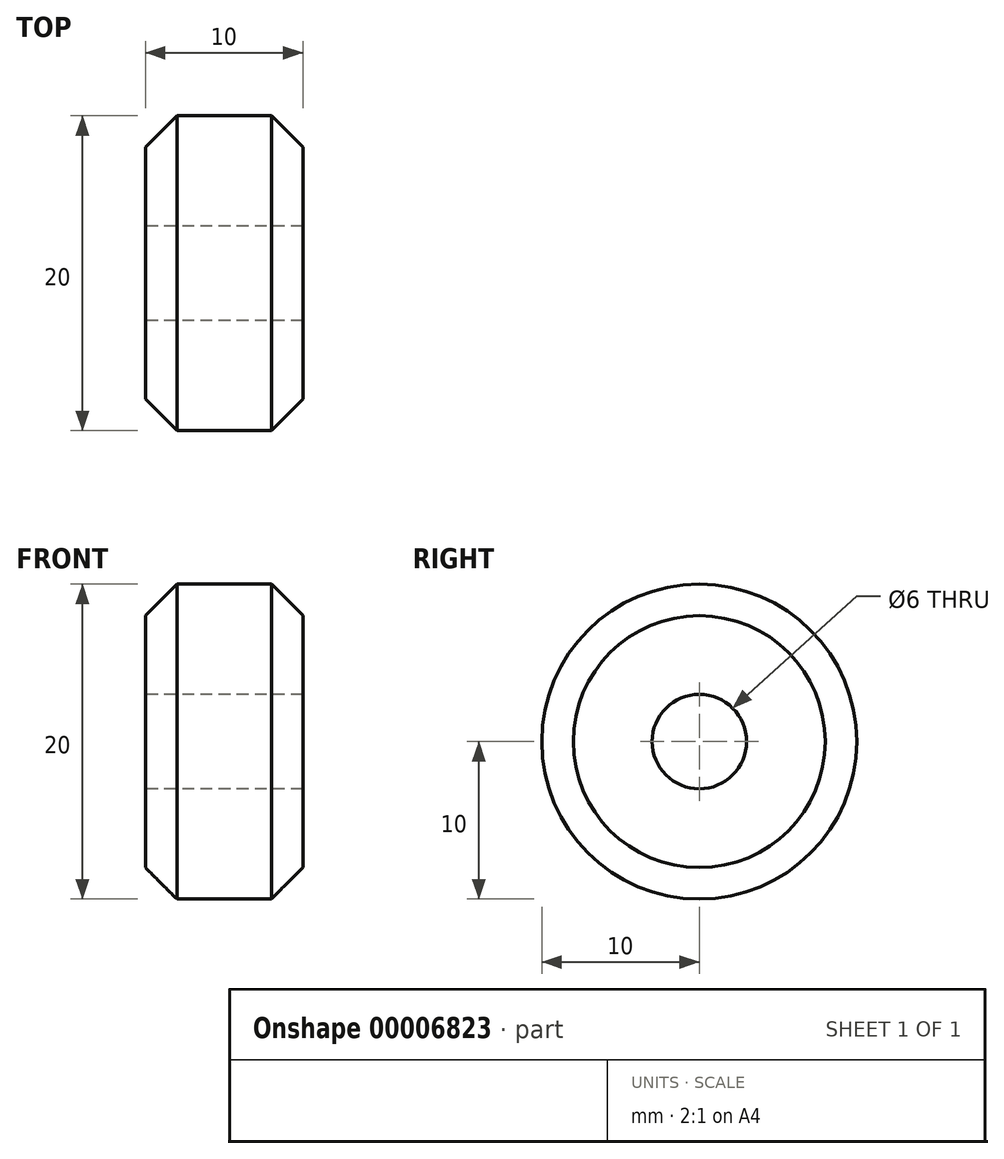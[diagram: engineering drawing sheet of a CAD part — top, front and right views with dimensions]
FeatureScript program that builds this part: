
annotation { "Feature Type Name" : "Feature", "Feature Type Description" : "" }
export const myFeature = defineFeature(function(context is Context, id is Id, definition is map)
    precondition{}
    {
        {
            var Q0;
            Q0=qCreatedBy(makeId("Right.planeOp"),FACE);
            var sketch = newSketch(context, id + "F0", { "sketchPlane" : qUnion([Q0])});
            skLineSegment(sketch, "E0", {"start": v(0, 0) * mm, "end": v(0, -3.09) * mm});
            skLineSegment(sketch, "E1", {"start": v(4.26, -9.53) * mm, "end": v(36, -23) * mm});
            skLineSegment(sketch, "E2", {"start": v(36, -23) * mm, "end": v(70, -23) * mm});
            skLineSegment(sketch, "E3", {"start": v(90, -3) * mm, "end": v(90, 47) * mm});
            skLineSegment(sketch, "E4", {"start": v(70, 67) * mm, "end": v(7, 67) * mm});
            skLineSegment(sketch, "E5", {"start": v(7, 67) * mm, "end": v(7, 45) * mm});
            skLineSegment(sketch, "E6", {"start": v(7, 45) * mm, "end": v(61, 45) * mm});
            skLineSegment(sketch, "E7", {"start": v(68, 38) * mm, "end": v(68, 4) * mm});
            skLineSegment(sketch, "E8", {"start": v(61, -3) * mm, "end": v(36, -3) * mm});
            skLineSegment(sketch, "E9", {"start": v(36, -3) * mm, "end": v(36, 0) * mm});
            skLineSegment(sketch, "E10", {"start": v(36, 0) * mm, "end": v(0, 0) * mm});
            skLineSegment(sketch, "E11", {"start": v(36, -23) * mm, "end": v(21.85, -23) * mm, "construction": true});
            skPoint(sketch, "E12.visualSharp", {"position": v(90, -23) * mm});
            skArc(sketch, "E12.filletArc", {"start": v(70, -23) * mm, "mid": v(84.14, -17.14) * mm, "end": v(90, -3) * mm});
            skPoint(sketch, "E13.visualSharp", {"position": v(90, 67) * mm});
            skArc(sketch, "E13.filletArc", {"start": v(90, 47) * mm, "mid": v(84.14, 61.14) * mm, "end": v(70, 67) * mm});
            skPoint(sketch, "E14.visualSharp", {"position": v(68, 45) * mm});
            skArc(sketch, "E14.filletArc", {"start": v(68, 38) * mm, "mid": v(65.95, 42.95) * mm, "end": v(61, 45) * mm});
            skPoint(sketch, "E15.visualSharp", {"position": v(68, -3) * mm});
            skArc(sketch, "E15.filletArc", {"start": v(61, -3) * mm, "mid": v(65.95, -0.95) * mm, "end": v(68, 4) * mm});
            skPoint(sketch, "E16.visualSharp", {"position": v(0, -7.72) * mm});
            skArc(sketch, "E16.filletArc", {"start": v(0, -3.09) * mm, "mid": v(1.16, -6.95) * mm, "end": v(4.26, -9.53) * mm});
            skSolve(sketch);
        }
        {
            var Q0;
            Q0=qSketchRegion(id+"F0",true);
            extrude(context, id + "F1", {"entities" : qUnion([Q0]), "endBound" : BoundingType.SYMMETRIC, "depth" : 20 * mm});
        }
        {
            var Q0;
            Q0=makeQuery(id+"F1.opExtrude","SWEPT_FACE",FACE,{"disambiguationData":[OSD([sQuery(id+"F0.wireOp",EDGE,"E6")])]});
            var sketch = newSketch(context, id + "F2", { "sketchPlane" : qUnion([Q0])});
            skCircle(sketch, "E17", {"center": v(0, -18) * mm, "radius": 11 * mm});
            skCircle(sketch, "E18", {"center": v(0, -18) * mm, "radius": 7 * mm});
            skSolve(sketch);
        }
        {
            var Q0;
            Q0=qSketchRegion(id+"F2",true);
            extrude(context, id + "F3", {"entities" : qUnion([Q0]), "operationType" : NewBodyOperationType.ADD, "oppositeDirection" : true, "depth" : 25 * mm});
        }
        {
            var Q0;
            Q0=makeQuery(id+"F3.boolean.opBoolean","SPLIT",FACE,{"disambiguationData":[TD([makeQuery(id+"F3.opExtrude","SWEPT_FACE",FACE,{"disambiguationData":[OSD([sQuery(id+"F2.wireOp",EDGE,"E18")])]})])],"derivedFrom":makeQuery(id+"F1.opExtrude","SWEPT_FACE",FACE,{"disambiguationData":[OSD([sQuery(id+"F0.wireOp",EDGE,"E4")])]})});
            var sketch = newSketch(context, id + "F4", { "sketchPlane" : qUnion([Q0])});
            skCircle(sketch, "E19.0", {"center": v(0, 18) * mm, "radius": 7 * mm});
            skSolve(sketch);
        }
        {
            var Q0;
            Q0=qSketchRegion(id+"F4",true);
            extrude(context, id + "F5", {"entities" : qUnion([Q0]), "operationType" : NewBodyOperationType.REMOVE, "oppositeDirection" : true, "depth" : 25 * mm});
        }
        {
            var Q0;
            {var subQ0=sQuery(id+"F0.wireOp",EDGE,"E4");var subQ1=makeQuery(id+"F1.opExtrude","SWEPT_FACE",FACE,{"disambiguationData":[OSD([subQ0])]});var subQ2=sQuery(id+"F0.wireOp",EDGE,"E5");Q0=makeQuery(id+"F3.boolean.opBoolean","SPLIT",FACE,{"disambiguationData":[TD([makeQuery(id+"F1.opExtrude","CAP_FACE",FACE,{"disambiguationData":[OSD([sQuery(id+"F0.wireOp",EDGE,"E0"),sQuery(id+"F0.wireOp",EDGE,"E1"),sQuery(id+"F0.wireOp",EDGE,"E2"),sQuery(id+"F0.wireOp",EDGE,"E3"),subQ0,subQ2,sQuery(id+"F0.wireOp",EDGE,"E6"),sQuery(id+"F0.wireOp",EDGE,"E7"),sQuery(id+"F0.wireOp",EDGE,"E8"),sQuery(id+"F0.wireOp",EDGE,"E9"),sQuery(id+"F0.wireOp",EDGE,"E10"),sQuery(id+"F0.wireOp",EDGE,"E12.filletArc"),sQuery(id+"F0.wireOp",EDGE,"E13.filletArc"),sQuery(id+"F0.wireOp",EDGE,"E14.filletArc"),sQuery(id+"F0.wireOp",EDGE,"E15.filletArc"),sQuery(id+"F0.wireOp",EDGE,"E16.filletArc")])],"isStart":false}),subQ1,makeQuery(id+"F1.opExtrude","SWEPT_FACE",FACE,{"disambiguationData":[OSD([subQ2])]}),makeQuery(id+"F3.opExtrude","SWEPT_FACE",FACE,{"disambiguationData":[OSD([sQuery(id+"F2.wireOp",EDGE,"E17")])]})])],"derivedFrom":subQ1});}
            var sketch = newSketch(context, id + "F6", { "sketchPlane" : qUnion([Q0])});
            skLineSegment(sketch, "E20.1.0", {"start": v(-10, 7) * mm, "end": v(0, 7) * mm});
            skArc(sketch, "E20.1.1", {"start": v(0, 7) * mm, "mid": v(-5.94, 8.74) * mm, "end": v(-10, 13.42) * mm});
            skLineSegment(sketch, "E20.1.2", {"start": v(-10, 13.42) * mm, "end": v(-10, 7) * mm});
            skSolve(sketch);
        }
        {
            var Q0;
            Q0=qSketchRegion(id+"F6",true);
            extrude(context, id + "F7", {"entities" : qUnion([Q0]), "operationType" : NewBodyOperationType.REMOVE, "oppositeDirection" : true, "depth" : 25 * mm});
        }
        {
            var Q0;
            {var subQ0=sQuery(id+"F0.wireOp",EDGE,"E4");var subQ1=makeQuery(id+"F1.opExtrude","SWEPT_FACE",FACE,{"disambiguationData":[OSD([subQ0])]});var subQ2=sQuery(id+"F0.wireOp",EDGE,"E5");Q0=makeQuery(id+"F3.boolean.opBoolean","SPLIT",FACE,{"disambiguationData":[TD([makeQuery(id+"F1.opExtrude","CAP_FACE",FACE,{"disambiguationData":[OSD([sQuery(id+"F0.wireOp",EDGE,"E0"),sQuery(id+"F0.wireOp",EDGE,"E1"),sQuery(id+"F0.wireOp",EDGE,"E2"),sQuery(id+"F0.wireOp",EDGE,"E3"),subQ0,subQ2,sQuery(id+"F0.wireOp",EDGE,"E6"),sQuery(id+"F0.wireOp",EDGE,"E7"),sQuery(id+"F0.wireOp",EDGE,"E8"),sQuery(id+"F0.wireOp",EDGE,"E9"),sQuery(id+"F0.wireOp",EDGE,"E10"),sQuery(id+"F0.wireOp",EDGE,"E12.filletArc"),sQuery(id+"F0.wireOp",EDGE,"E13.filletArc"),sQuery(id+"F0.wireOp",EDGE,"E14.filletArc"),sQuery(id+"F0.wireOp",EDGE,"E15.filletArc"),sQuery(id+"F0.wireOp",EDGE,"E16.filletArc")])],"isStart":false}),subQ1,makeQuery(id+"F1.opExtrude","SWEPT_FACE",FACE,{"disambiguationData":[OSD([subQ2])]}),makeQuery(id+"F3.opExtrude","SWEPT_FACE",FACE,{"disambiguationData":[OSD([sQuery(id+"F2.wireOp",EDGE,"E17")])]})])],"derivedFrom":subQ1});}
            var sketch = newSketch(context, id + "F8", { "sketchPlane" : qUnion([Q0])});
            skArc(sketch, "E21.0", {"start": v(10, 13.42) * mm, "mid": v(5.94, 8.74) * mm, "end": v(0, 7) * mm});
            skLineSegment(sketch, "E22", {"start": v(10, 13.42) * mm, "end": v(10, 7) * mm});
            skLineSegment(sketch, "E23", {"start": v(10, 7) * mm, "end": v(0, 7) * mm});
            skSolve(sketch);
        }
        {
            var Q0;
            Q0=qSketchRegion(id+"F8",true);
            extrude(context, id + "F9", {"entities" : qUnion([Q0]), "operationType" : NewBodyOperationType.REMOVE, "oppositeDirection" : true, "depth" : 25 * mm});
        }
        {
            var Q0;
            Q0=makeQuery(id+"F1.opExtrude","SWEPT_EDGE",EDGE,{"disambiguationData":[OSD([sQuery(id+"F0.wireOp",EDGE,"E8"),sQuery(id+"F0.wireOp",EDGE,"E9")])]});
            fillet(context, id + "F10", {"entities" : qUnion([Q0]), "radius" : 3 * mm, "tangentPropagation" : true, "allowEdgeOverflow" : false});
        }
        {
            var Q0;
            Q0=qCreatedBy(makeId("Right.planeOp"),FACE);
            var sketch = newSketch(context, id + "F11", { "sketchPlane" : qUnion([Q0])});
            skLineSegment(sketch, "E24", {"start": v(11, 100) * mm, "end": v(7, 100) * mm});
            skLineSegment(sketch, "E25", {"start": v(7, 100) * mm, "end": v(7, 118) * mm});
            skLineSegment(sketch, "E26", {"start": v(7, 118) * mm, "end": v(18, 118) * mm});
            skLineSegment(sketch, "E27", {"start": v(18, 118) * mm, "end": v(18, 35) * mm});
            skLineSegment(sketch, "E28", {"start": v(11, 100) * mm, "end": v(11, 35) * mm});
            skLineSegment(sketch, "E29", {"start": v(11, 35) * mm, "end": v(18, 35) * mm});
            skSolve(sketch);
        }
        {
            var Q0;
            Q0=qSketchRegion(id+"F11",true);
            var Q1;
            Q1=sQuery(id+"F11.wireOp",EDGE,"E27");
            revolve(context, id + "F12", {"entities" : qUnion([Q0]), "axis" : qUnion([Q1]), "revolveType" : RevolveType.FULL});
        }
        {
            var Q0;
            Q0=makeQuery(id+"F12.opRevolve","SWEPT_EDGE",EDGE,{"disambiguationData":[OSD([sQuery(id+"F11.wireOp",EDGE,"E25"),sQuery(id+"F11.wireOp",EDGE,"E26")])]});
            chamfer(context, id + "F13", {"entities" : qUnion([Q0]), "width" : 2 * mm, "tangentPropagation" : true});
        }
        {
            var Q0;
            Q0=makeQuery(id+"F12.opRevolve","SWEPT_FACE",FACE,{"disambiguationData":[OSD([sQuery(id+"F11.wireOp",EDGE,"E29")])]});
            var sketch = newSketch(context, id + "F14", { "sketchPlane" : qUnion([Q0])});
            skCircle(sketch, "E30", {"center": v(0, -18) * mm, "radius": 5 * mm});
            skSolve(sketch);
        }
        {
            var Q0;
            Q0=qSketchRegion(id+"F14",true);
            extrude(context, id + "F15", {"entities" : qUnion([Q0]), "operationType" : NewBodyOperationType.ADD, "depth" : 2 * mm});
        }
        {
            var Q0;
            Q0=makeQuery(id+"F15.opExtrude","CAP_FACE",FACE,{"disambiguationData":[OSD([sQuery(id+"F14.wireOp",EDGE,"E30")])],"isStart":false});
            var sketch = newSketch(context, id + "F16", { "sketchPlane" : qUnion([Q0])});
            skCircle(sketch, "E31", {"center": v(0, -18) * mm, "radius": 3 * mm});
            skSolve(sketch);
        }
        {
            var Q0;
            Q0=qSketchRegion(id+"F16",true);
            extrude(context, id + "F17", {"entities" : qUnion([Q0]), "operationType" : NewBodyOperationType.ADD, "depth" : 8 * mm});
        }
        {
            var Q0;
            Q0=qCreatedBy(makeId("Right.planeOp"),FACE);
            var sketch = newSketch(context, id + "F18", { "sketchPlane" : qUnion([Q0])});
            skCircle(sketch, "E32", {"center": v(18, 109) * mm, "radius": 5 * mm});
            skSolve(sketch);
        }
        {
            var Q0;
            Q0=qSketchRegion(id+"F18",true);
            extrude(context, id + "F19", {"entities" : qUnion([Q0]), "operationType" : NewBodyOperationType.REMOVE, "oppositeDirection" : true, "depth" : 25 * mm});
        }
        {
            var Q0;
            Q0=makeQuery(id+"F19.boolean.opBoolean","COPY",FACE,{"derivedFrom":makeQuery(id+"F19.opExtrude","CAP_FACE",FACE,{"disambiguationData":[OSD([sQuery(id+"F18.wireOp",EDGE,"E32")])],"isStart":true})});
            var sketch = newSketch(context, id + "F20", { "sketchPlane" : qUnion([Q0])});
            skCircle(sketch, "E33.0", {"center": v(-18, 109) * mm, "radius": 5 * mm});
            skSolve(sketch);
        }
        {
            var Q0;
            Q0=qSketchRegion(id+"F20",true);
            extrude(context, id + "F21", {"entities" : qUnion([Q0]), "operationType" : NewBodyOperationType.REMOVE, "oppositeDirection" : true, "depth" : 25 * mm});
        }
        {
            var Q0;
            Q0=qCreatedBy(makeId("Right.planeOp"),FACE);
            var sketch = newSketch(context, id + "F22", { "sketchPlane" : qUnion([Q0])});
            skCircle(sketch, "E34.0", {"center": v(18, 109) * mm, "radius": 5 * mm});
            skSolve(sketch);
        }
        {
            var Q0;
            Q0=qSketchRegion(id+"F22",true);
            extrude(context, id + "F23", {"entities" : qUnion([Q0]), "endBound" : BoundingType.SYMMETRIC, "depth" : 89 * mm});
        }
        {
            var Q0;
            Q0=makeQuery(id+"F23.opExtrude","CAP_FACE",FACE,{"disambiguationData":[OSD([sQuery(id+"F22.wireOp",EDGE,"E34.0")])],"isStart":false});
            var sketch = newSketch(context, id + "F24", { "sketchPlane" : qUnion([Q0])});
            skCircle(sketch, "E35", {"center": v(18, 109) * mm, "radius": 3 * mm});
            skSolve(sketch);
        }
        {
            var Q0;
            Q0=qSketchRegion(id+"F24",true);
            extrude(context, id + "F25", {"entities" : qUnion([Q0]), "operationType" : NewBodyOperationType.ADD, "depth" : 12 * mm});
        }
        {
            var Q0;
            Q0=makeQuery(id+"F23.opExtrude","CAP_FACE",FACE,{"disambiguationData":[OSD([sQuery(id+"F22.wireOp",EDGE,"E34.0")])],"isStart":true});
            var sketch = newSketch(context, id + "F26", { "sketchPlane" : qUnion([Q0])});
            skCircle(sketch, "E36", {"center": v(-18, 109) * mm, "radius": 3 * mm});
            skSolve(sketch);
        }
        {
            var Q0;
            Q0=qSketchRegion(id+"F26",true);
            extrude(context, id + "F27", {"entities" : qUnion([Q0]), "operationType" : NewBodyOperationType.ADD, "depth" : 12 * mm});
        }
        {
            var Q0;
            Q0=makeQuery(id+"F25.opExtrude","CAP_FACE",FACE,{"disambiguationData":[OSD([sQuery(id+"F24.wireOp",EDGE,"E35")])],"isStart":false});
            var sketch = newSketch(context, id + "F28", { "sketchPlane" : qUnion([Q0])});
            skCircle(sketch, "E37.0", {"center": v(18, 109) * mm, "radius": 3 * mm});
            skCircle(sketch, "E38", {"center": v(18, 109) * mm, "radius": 10 * mm});
            skSolve(sketch);
        }
        {
            var Q0;
            Q0=qSketchRegion(id+"F28",true);
            extrude(context, id + "F29", {"entities" : qUnion([Q0]), "oppositeDirection" : true, "depth" : 10 * mm});
        }
        {
            var Q0;
            Q0=makeQuery(id+"F29.opExtrude","CAP_EDGE",EDGE,{"disambiguationData":[OSD([sQuery(id+"F28.wireOp",EDGE,"E38")])],"isStart":true});
            var Q1;
            Q1=makeQuery(id+"F29.opExtrude","CAP_EDGE",EDGE,{"disambiguationData":[OSD([sQuery(id+"F28.wireOp",EDGE,"E38")])],"isStart":false});
            chamfer(context, id + "F30", {"entities" : qUnion([Q0, Q1]), "width" : 2 * mm, "tangentPropagation" : true});
        }
        {
            var Q0;
            Q0=makeQuery(id+"F29.opExtrude","SWEPT_BODY",BODY,{"disambiguationData":[OSD([sQuery(id+"F28.wireOp",EDGE,"E37.0"),sQuery(id+"F28.wireOp",EDGE,"E38")])]});
            var Q1;
            Q1=qCreatedBy(makeId("Right.planeOp"),FACE);
            mirror(context, id + "F31", {"entities" : qUnion([Q0]), "mirrorPlane" : qUnion([Q1])});
        }
        {
            var Q0;
            Q0=qCreatedBy(makeId("Right.planeOp"),FACE);
            var sketch = newSketch(context, id + "F32", { "sketchPlane" : qUnion([Q0])});
            skLineSegment(sketch, "E39", {"start": v(21, 30) * mm, "end": v(21, 32) * mm});
            skLineSegment(sketch, "E40", {"start": v(34.36, 22) * mm, "end": v(36.5, 22) * mm});
            skArc(sketch, "E41", {"start": v(36.5, 22) * mm, "mid": v(30.47, 29.67) * mm, "end": v(21, 32) * mm});
            skArc(sketch, "E42.0", {"start": v(34.36, 22) * mm, "mid": v(29, 28.23) * mm, "end": v(21, 30) * mm});
            skLineSegment(sketch, "E43", {"start": v(18, 24.98) * mm, "end": v(18, 32) * mm});
            skSolve(sketch);
        }
        {
            var Q0;
            Q0=qSketchRegion(id+"F32",true);
            var Q1;
            Q1=sQuery(id+"F32.wireOp",EDGE,"E43");
            revolve(context, id + "F33", {"entities" : qUnion([Q0]), "axis" : qUnion([Q1]), "revolveType" : RevolveType.FULL});
        }
        {
            var Q0;
            Q0=makeQuery(id+"F1.opExtrude","SWEPT_BODY",BODY,{"disambiguationData":[OSD([sQuery(id+"F0.wireOp",EDGE,"E0"),sQuery(id+"F0.wireOp",EDGE,"E1"),sQuery(id+"F0.wireOp",EDGE,"E2"),sQuery(id+"F0.wireOp",EDGE,"E3"),sQuery(id+"F0.wireOp",EDGE,"E4"),sQuery(id+"F0.wireOp",EDGE,"E5"),sQuery(id+"F0.wireOp",EDGE,"E6"),sQuery(id+"F0.wireOp",EDGE,"E7"),sQuery(id+"F0.wireOp",EDGE,"E8"),sQuery(id+"F0.wireOp",EDGE,"E9"),sQuery(id+"F0.wireOp",EDGE,"E10"),sQuery(id+"F0.wireOp",EDGE,"E12.filletArc"),sQuery(id+"F0.wireOp",EDGE,"E13.filletArc"),sQuery(id+"F0.wireOp",EDGE,"E14.filletArc"),sQuery(id+"F0.wireOp",EDGE,"E15.filletArc"),sQuery(id+"F0.wireOp",EDGE,"E16.filletArc")])]});
            deleteBodies(context, id + "F34", {"entities" : qUnion([Q0])});
        }
        {
            var Q0;
            Q0=makeQuery(id+"F12.opRevolve","SWEPT_BODY",BODY,{"disambiguationData":[OSD([sQuery(id+"F11.wireOp",EDGE,"E24"),sQuery(id+"F11.wireOp",EDGE,"E25"),sQuery(id+"F11.wireOp",EDGE,"E26"),sQuery(id+"F11.wireOp",EDGE,"E27"),sQuery(id+"F11.wireOp",EDGE,"E28"),sQuery(id+"F11.wireOp",EDGE,"E29")])]});
            deleteBodies(context, id + "F35", {"entities" : qUnion([Q0])});
        }
        {
            var Q0;
            Q0=makeQuery(id+"F23.opExtrude","SWEPT_BODY",BODY,{"disambiguationData":[OSD([sQuery(id+"F22.wireOp",EDGE,"E34.0")])]});
            deleteBodies(context, id + "F36", {"entities" : qUnion([Q0])});
        }
        {
            var Q0;
            Q0=makeQuery(id+"F33.opRevolve","SWEPT_BODY",BODY,{"disambiguationData":[OSD([sQuery(id+"F32.wireOp",EDGE,"E39"),sQuery(id+"F32.wireOp",EDGE,"E40"),sQuery(id+"F32.wireOp",EDGE,"E41"),sQuery(id+"F32.wireOp",EDGE,"E42.0")])]});
            deleteBodies(context, id + "F37", {"entities" : qUnion([Q0])});
        }
        {
            var Q0;
            Q0=makeQuery(id+"F29.opExtrude","SWEPT_BODY",BODY,{"disambiguationData":[OSD([sQuery(id+"F28.wireOp",EDGE,"E37.0"),sQuery(id+"F28.wireOp",EDGE,"E38")])]});
            deleteBodies(context, id + "F38", {"entities" : qUnion([Q0])});
        }
    });
